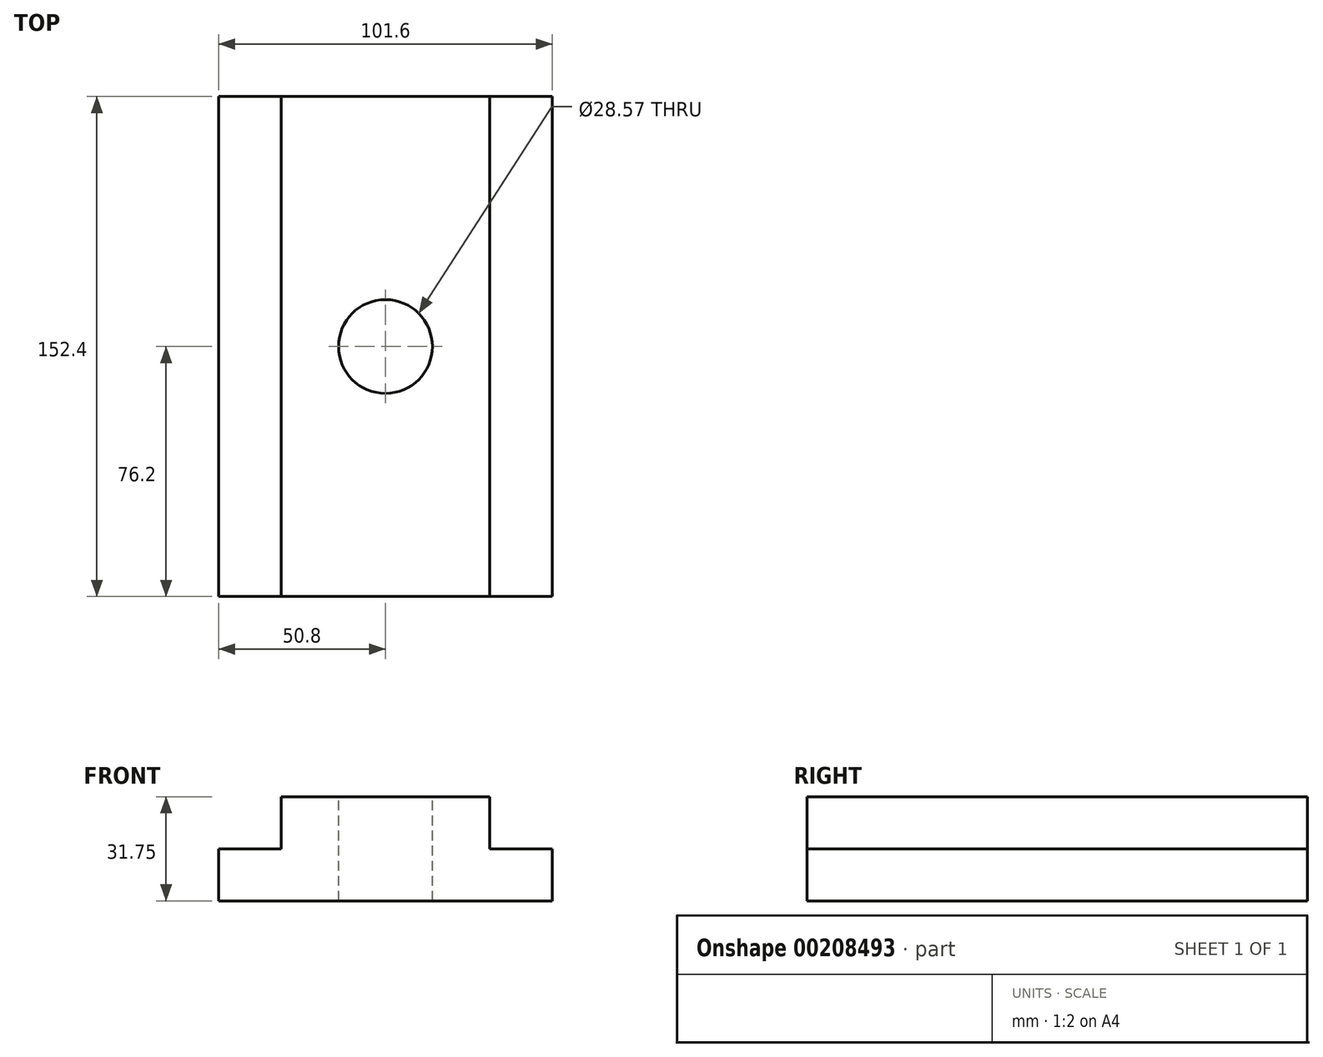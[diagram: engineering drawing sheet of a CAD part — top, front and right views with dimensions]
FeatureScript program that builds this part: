
annotation { "Feature Type Name" : "Feature", "Feature Type Description" : "" }
export const myFeature = defineFeature(function(context is Context, id is Id, definition is map)
    precondition{}
    {
        {
            var Q0;
            Q0=qCreatedBy(makeId("Front.planeOp"),FACE);
            var sketch = newSketch(context, id + "F0", { "sketchPlane" : qUnion([Q0])});
            skLineSegment(sketch, "E0", {"start": v(19.97, 35.75) * mm, "end": v(-43.53, 35.75) * mm});
            skLineSegment(sketch, "E1", {"start": v(-43.53, 35.75) * mm, "end": v(-43.53, 19.88) * mm});
            skLineSegment(sketch, "E2", {"start": v(-43.53, 19.88) * mm, "end": v(-62.58, 19.88) * mm});
            skLineSegment(sketch, "E3", {"start": v(-62.58, 19.88) * mm, "end": v(-62.58, 4) * mm});
            skLineSegment(sketch, "E4", {"start": v(-62.58, 4) * mm, "end": v(39.02, 4) * mm});
            skLineSegment(sketch, "E5", {"start": v(39.02, 4) * mm, "end": v(39.02, 19.88) * mm});
            skLineSegment(sketch, "E6", {"start": v(39.02, 19.88) * mm, "end": v(20, 19.88) * mm});
            skLineSegment(sketch, "E7", {"start": v(19.97, 35.75) * mm, "end": v(20, 19.88) * mm});
            skSolve(sketch);
        }
        {
            var Q0;
            Q0 = qSketchRegion(id + "F0", true);
            extrude(context, id + "F1", {"entities" : qUnion([Q0]), "depth" : 152.4 * mm});
        }
        {
            var Q0;
            Q0=makeQuery(id+"F1.opExtrude","SWEPT_FACE",FACE,{"disambiguationData":[OSD([sQuery(id+"F0.wireOp",EDGE,"E0")])]});
            var sketch = newSketch(context, id + "F2", { "sketchPlane" : qUnion([Q0])});
            skCircle(sketch, "E8", {"center": v(-11.78, -76.2) * mm, "radius": 14.29 * mm});
            skSolve(sketch);
        }
        {
            var Q0;
            Q0 = qSketchRegion(id + "F2", true);
            extrude(context, id + "F3", {"entities" : qUnion([Q0]), "operationType" : NewBodyOperationType.REMOVE, "endBound" : BoundingType.THROUGH_ALL, "oppositeDirection" : true, "depth" : 25.4 * mm});
        }
    });
